# Revit family: PRD_AR_PllrTps_F7EElectronicPillarTap_F7EV1001_F7EV1002
name_source: partatom
category: Plumbing Fixtures
units: mm (PartAtom-declared; Revit-internal decimal feet)

## family parameters
Always vertical = Yes
Cut with Voids When Loaded = No
Enable Cutting in Views = No
Maintain Annotation Orientation = No
OmniClass Number = 23.45.55.14
OmniClass Title = Single Faucets
Part Type = Normal
Room Calculation Point = No
Round Connector Dimension = Use Diameter
Shared = No
Work Plane-Based = Yes

## types (2) — shared parameters
AccentColour = None
AssetType = Fixed
BasicColour = Stainless steel-look
BodyMaterial = PRD_AR_StainlessSteel_Brushed
Category = Pr_40_20_87_60, Pillar taps
CloseOffRating = 0.0 Pa
Color = stainless steel-look
CompatibleA3000Open = Yes
Default Elevation = 1219 mm
DefaultAutomaticHygieneFlush = 24h after the last activity
Depressurised = No
DiameterNominal = DN15
Export Type to IFC As = IfcValveType
FaucetFunction = MIXED
FaucetOperation = SELFCLOSING
FaucetTopDescription = opto-electronically controlled
FaucetType = PILLAR
Finish = brushed surface
FlowColdWater = 0.0 L/s
FunctionalPrinciple = electronic self-closing
HygieneFlushing = Yes
IfcExportAs = IfcValveType
IfcExportType = FAUCET
InletSize = G 3/8
LockingMechanism = Top section, non-ceramic
Manufacturer = KWC Group Management AG
ManufacturerName = KWC Group Management AG
ManufacturerURL = www.kwc-professional.com
Material = stainless steel
MaterialFitting = Stainless Steel
MinimumFlowPressure = 1 bar
NBSDescription = Taps and water supply fittings for bath
NBSReference = 45-35-70/345
Parameterization = Remote Control
PopUpWasteSet = No
PositionOfPowerConnection = From Bottom
PowerSupplyConnection = 6,75 / 12 V DC / A3000 open
ProductInformation = http://pim.kwc.com
ProtectiveShutdown = Yes
Shape = Pillar tap
Size = 15
SoundInsulation = No
Spout = Fixed
Status = New
SurfaceFinishFitting = Brushed
SurfaceTreatmentFitting = Brushed
TemperatureLimit = No
TestPressure = 0.0 Pa
ThermalDisinfection = No
Type IFC Predefined Type = FAUCET
TypeOfMixing = No
TypeOfMounting = Tap Hole
TypeOfOperation = Sensor Operation
TypeOfPowerSupply = Other
TypeOfSensor = Opto-electronic sensor
TypeOfTap = Pillar Tap
URL = www.kwc-professional.com
Uniclass2015Code = Pr_40_20_87_60
Uniclass2015Title = Pillar taps
Uniclass2015Version = Products v1.36
ValveMechanism = OTHER
ValveOperation = SOLENOID
ValvePattern = STRAIGHT_2_PORT
Version = 1
Voltage = 12 V
WaterConnection = Hose (gland nut)
WithBackflowPreventer = No
WithFilter = Yes
WithRosettesOrCoverPlate = No
WithTransformer = No
WorkingPressure = 0.0 Pa
zero-valued in all types: FlowCoefficient, NominalDepth, NominalWidth

## per-type parameters (varying)
| type | BIMObjectName | Description | F7EV1001 | F7EV1002 | Features | ModelNumber | Name | NominalHeight |
| F7EV1001 | PRD_AR_PillarTaps_F7EElectronicPillarTap_F7EV1001 | F7E pillar tap DN 15 for sanitary facilities, opto-electronically controlled. For connection to pre-mixed hot or cold water via hose and strainer. Control electronics, solenoid valve and sensor in stainless steel housing, brushed surface, outlet height 115 mm and projection 125 mm. Angle-adjustable and anti-theft aerator with integrated flow regulator 5.7 l/min. Activated water hygiene flushing 24 hours after last activation, safety switch-off with continuous reflection and saving of statistical data. With option for parameterization and communication via optional bidirectional remote control or C module with the necessary app. Optionally for battery operation with battery compartment including 6 V lithium battery (CR-P2) per fitting, for installation below the washbasin, or for separate power supply via power supply unit 6.75 V/12 V DC or AQUA 3000 open system accessories.

Battery compartment including battery or power supply unit with extension cable must be ordered separately. | Yes | No | For connection to pre-mixed hot or cold water via hose and strainer. Control electronics, solenoid valve and sensor in stainless steel housing, brushed surface, outlet height 115 mm and projection 125 mm. | 3600001255 | F7E Electronic pillar tap F7EV1001 | 165 mm  [stored 0.541339 ft] |
| F7EV1002 | PRD_AR_PillarTaps_F7EElectronicPillarTap_F7EV1002 | F7E pillar tap DN 15 for sanitary facilities, opto-electronically controlled. For connection to pre-mixed hot or cold water via hose and strainer. Control electronics, solenoid valve and sensor in stainless steel housing, brushed surface, outlet height 245 mm and projection 180 mm. Angle-adjustable and anti-theft aerator with integrated flow regulator 5.7 l/min. Activated water hygiene flushing 24 hours after last activation, safety switch-off with continuous reflection and saving of statistical data. With option for parameterization and communication via optional bidirectional remote control or C module with the necessary app. Optionally for battery operation with battery compartment including 6 V lithium battery (CR-P2) per fitting, for installation below the washbasin, or for separate power supply via power supply unit 6.75 V/12 V DC or AQUA 3000 open system accessories.

Battery compartment including battery or power supply unit with extension cable must be ordered separately. | No | Yes | For connection to pre-mixed hot or cold water via hose and strainer. Control electronics, solenoid valve and sensor in stainless steel housing, brushed surface, outlet height 245 mm and projection 180 mm. | 3600001258 | F7E Electronic pillar tap F7EV1002 | 295 mm  [stored 0.967848 ft] |

note: column(s) folded — value = type name in every type: Model, ModelReference

note: [stored X ft] marks values corroborated as IEEE doubles in the binary element streams (Revit-internal decimal feet)

## geometry (parser evidence)
native form markers: Sweep x5
no freeform markers — native parametric forms only
